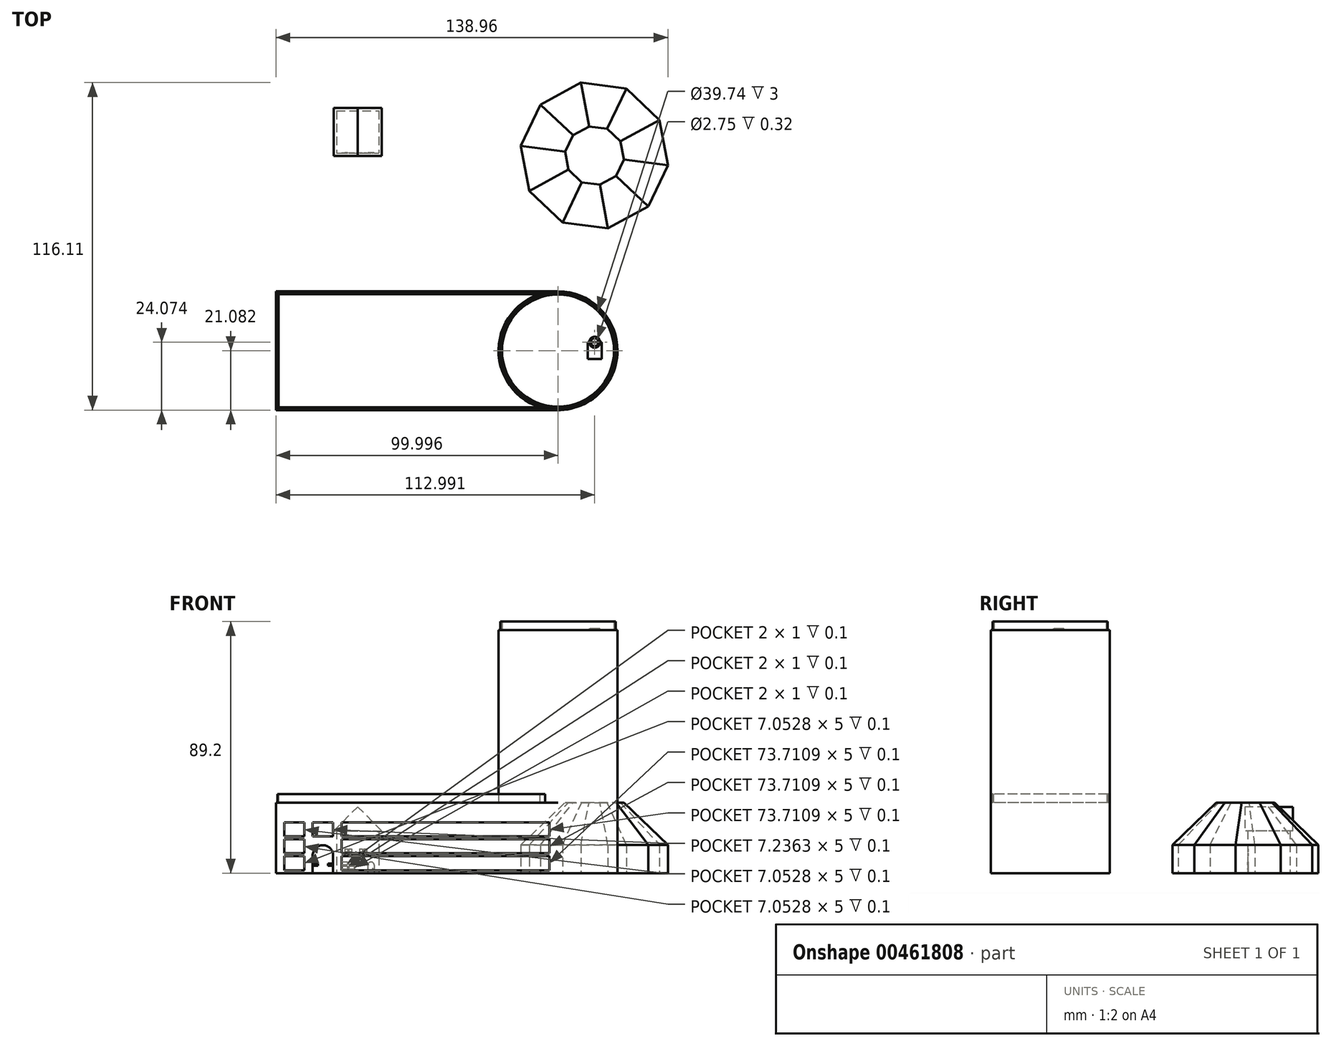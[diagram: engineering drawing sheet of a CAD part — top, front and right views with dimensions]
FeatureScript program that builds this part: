
annotation { "Feature Type Name" : "Feature", "Feature Type Description" : "" }
export const myFeature = defineFeature(function(context is Context, id is Id, definition is map)
    precondition{}
    {
        {
            var Q0;
            Q0=qCreatedBy(makeId("Top.planeOp"),FACE);
            var sketch = newSketch(context, id + "F0", { "sketchPlane" : qUnion([Q0])});
            skLineSegment(sketch, "E0.bottom", {"start": v(-51.13, 45.78) * mm, "end": v(-36.13, 45.78) * mm});
            skLineSegment(sketch, "E0.top", {"start": v(-51.13, 30.78) * mm, "end": v(-36.13, 30.78) * mm});
            skLineSegment(sketch, "E0.left", {"start": v(-51.13, 45.78) * mm, "end": v(-51.13, 30.78) * mm});
            skLineSegment(sketch, "E0.right", {"start": v(-36.13, 45.78) * mm, "end": v(-36.13, 30.78) * mm});
            skSolve(sketch);
        }
        {
            var Q0;
            Q0=makeQuery(id+"F0.imprint","IMPRINT",FACE,{"disambiguationData":[TD([[makeQuery(id+"F0.imprint","IMPRINT",EDGE,{"derivedFrom":sQuery(id+"F0.wireOp",EDGE,"E0.bottom")}),-1.0]])]});
            extrude(context, id + "F1", {"entities" : qUnion([Q0]), "depth" : 15 * mm});
        }
        {
            var Q0;
            Q0=makeQuery(id+"F1.opExtrude","SWEPT_FACE",FACE,{"disambiguationData":[OSD([sQuery(id+"F0.wireOp",EDGE,"E0.top")])]});
            var sketch = newSketch(context, id + "F2", { "sketchPlane" : qUnion([Q0])});
            skLineSegment(sketch, "E1.bottom", {"start": v(-49.33, 3.96) * mm, "end": v(-47.33, 3.96) * mm});
            skLineSegment(sketch, "E1.top", {"start": v(-49.33, 2.96) * mm, "end": v(-47.33, 2.96) * mm});
            skLineSegment(sketch, "E1.left", {"start": v(-49.33, 3.96) * mm, "end": v(-49.33, 2.96) * mm});
            skLineSegment(sketch, "E1.right", {"start": v(-47.33, 3.96) * mm, "end": v(-47.33, 2.96) * mm});
            skLineSegment(sketch, "E2.bottom", {"start": v(-46.83, 3.96) * mm, "end": v(-44.83, 3.96) * mm});
            skLineSegment(sketch, "E2.top", {"start": v(-46.83, 2.96) * mm, "end": v(-44.83, 2.96) * mm});
            skLineSegment(sketch, "E2.left", {"start": v(-46.83, 3.96) * mm, "end": v(-46.83, 2.96) * mm});
            skLineSegment(sketch, "E2.right", {"start": v(-44.83, 3.96) * mm, "end": v(-44.83, 2.96) * mm});
            skLineSegment(sketch, "E3.bottom", {"start": v(-49.33, 2.46) * mm, "end": v(-47.33, 2.46) * mm});
            skLineSegment(sketch, "E3.top", {"start": v(-49.33, 1.46) * mm, "end": v(-47.33, 1.46) * mm});
            skLineSegment(sketch, "E3.left", {"start": v(-49.33, 2.46) * mm, "end": v(-49.33, 1.46) * mm});
            skLineSegment(sketch, "E3.right", {"start": v(-47.33, 2.46) * mm, "end": v(-47.33, 1.46) * mm});
            skLineSegment(sketch, "E4.bottom", {"start": v(-46.83, 2.46) * mm, "end": v(-44.83, 2.46) * mm});
            skLineSegment(sketch, "E4.top", {"start": v(-46.83, 1.46) * mm, "end": v(-44.83, 1.46) * mm});
            skLineSegment(sketch, "E4.left", {"start": v(-46.83, 2.46) * mm, "end": v(-46.83, 1.46) * mm});
            skLineSegment(sketch, "E4.right", {"start": v(-44.83, 2.46) * mm, "end": v(-44.83, 1.46) * mm});
            skLineSegment(sketch, "E5.bottom", {"start": v(-48.24, 8.6) * mm, "end": v(-47.24, 8.6) * mm});
            skLineSegment(sketch, "E5.top", {"start": v(-48.24, 7.6) * mm, "end": v(-47.24, 7.6) * mm});
            skLineSegment(sketch, "E5.left", {"start": v(-48.24, 8.6) * mm, "end": v(-48.24, 7.6) * mm});
            skLineSegment(sketch, "E5.right", {"start": v(-47.24, 8.6) * mm, "end": v(-47.24, 7.6) * mm});
            skLineSegment(sketch, "E6.bottom", {"start": v(-46.75, 8.6) * mm, "end": v(-45.75, 8.6) * mm});
            skLineSegment(sketch, "E6.top", {"start": v(-46.75, 7.6) * mm, "end": v(-45.75, 7.6) * mm});
            skLineSegment(sketch, "E6.left", {"start": v(-46.75, 8.6) * mm, "end": v(-46.75, 7.6) * mm});
            skLineSegment(sketch, "E6.right", {"start": v(-45.75, 8.6) * mm, "end": v(-45.75, 7.6) * mm});
            skLineSegment(sketch, "E7.bottom", {"start": v(-47.25, 7.1) * mm, "end": v(-48.25, 7.1) * mm});
            skLineSegment(sketch, "E7.top", {"start": v(-47.25, 6.1) * mm, "end": v(-48.25, 6.1) * mm});
            skLineSegment(sketch, "E7.left", {"start": v(-47.25, 7.1) * mm, "end": v(-47.25, 6.1) * mm});
            skLineSegment(sketch, "E7.right", {"start": v(-48.25, 7.1) * mm, "end": v(-48.25, 6.1) * mm});
            skLineSegment(sketch, "E8.bottom", {"start": v(-46.75, 7.1) * mm, "end": v(-45.75, 7.1) * mm});
            skLineSegment(sketch, "E8.top", {"start": v(-46.75, 6.1) * mm, "end": v(-45.75, 6.1) * mm});
            skLineSegment(sketch, "E8.left", {"start": v(-46.75, 7.1) * mm, "end": v(-46.75, 6.1) * mm});
            skLineSegment(sketch, "E8.right", {"start": v(-45.75, 7.1) * mm, "end": v(-45.75, 6.1) * mm});
            skLineSegment(sketch, "E9.bottom", {"start": v(-42.98, 8.6) * mm, "end": v(-41.98, 8.6) * mm});
            skLineSegment(sketch, "E9.top", {"start": v(-42.98, 7.6) * mm, "end": v(-41.98, 7.6) * mm});
            skLineSegment(sketch, "E9.left", {"start": v(-42.98, 8.6) * mm, "end": v(-42.98, 7.6) * mm});
            skLineSegment(sketch, "E9.right", {"start": v(-41.98, 8.6) * mm, "end": v(-41.98, 7.6) * mm});
            skLineSegment(sketch, "E10.bottom", {"start": v(-41.48, 8.6) * mm, "end": v(-40.48, 8.6) * mm});
            skLineSegment(sketch, "E10.top", {"start": v(-41.48, 7.6) * mm, "end": v(-40.48, 7.6) * mm});
            skLineSegment(sketch, "E10.left", {"start": v(-41.48, 8.6) * mm, "end": v(-41.48, 7.6) * mm});
            skLineSegment(sketch, "E10.right", {"start": v(-40.48, 8.6) * mm, "end": v(-40.48, 7.6) * mm});
            skLineSegment(sketch, "E11.bottom", {"start": v(-42.98, 7.1) * mm, "end": v(-41.98, 7.1) * mm});
            skLineSegment(sketch, "E11.top", {"start": v(-42.98, 6.1) * mm, "end": v(-41.98, 6.1) * mm});
            skLineSegment(sketch, "E11.left", {"start": v(-42.98, 7.1) * mm, "end": v(-42.98, 6.1) * mm});
            skLineSegment(sketch, "E11.right", {"start": v(-41.98, 7.1) * mm, "end": v(-41.98, 6.1) * mm});
            skLineSegment(sketch, "E12.bottom", {"start": v(-41.48, 7.1) * mm, "end": v(-40.48, 7.1) * mm});
            skLineSegment(sketch, "E12.top", {"start": v(-41.48, 6.1) * mm, "end": v(-40.48, 6.1) * mm});
            skLineSegment(sketch, "E12.left", {"start": v(-41.48, 7.1) * mm, "end": v(-41.48, 6.1) * mm});
            skLineSegment(sketch, "E12.right", {"start": v(-40.48, 7.1) * mm, "end": v(-40.48, 6.1) * mm});
            skLineSegment(sketch, "E13", {"start": v(-40.05, 2.82) * mm, "end": v(-40.05, 0) * mm});
            skLineSegment(sketch, "E14", {"start": v(-37.79, 2.82) * mm, "end": v(-37.79, 0) * mm});
            skArc(sketch, "E15", {"start": v(-37.79, 2.82) * mm, "mid": v(-38.92, 3.95) * mm, "end": v(-40.05, 2.82) * mm});
            skCircle(sketch, "E16", {"center": v(-38.3, 1.47) * mm, "radius": 0.17 * mm});
            skSolve(sketch);
        }
        {
            var Q0;
            Q0=makeQuery(id+"F2.imprint","IMPRINT",FACE,{"disambiguationData":[TD([[makeQuery(id+"F2.imprint","IMPRINT",EDGE,{"derivedFrom":sQuery(id+"F2.wireOp",EDGE,"E2.bottom")}),-1.0]])]});
            var Q1;
            Q1=makeQuery(id+"F2.imprint","IMPRINT",FACE,{"disambiguationData":[TD([[makeQuery(id+"F2.imprint","IMPRINT",EDGE,{"derivedFrom":sQuery(id+"F2.wireOp",EDGE,"E3.bottom")}),-1.0]])]});
            var Q2;
            Q2=makeQuery(id+"F2.imprint","IMPRINT",FACE,{"disambiguationData":[TD([[makeQuery(id+"F2.imprint","IMPRINT",EDGE,{"derivedFrom":sQuery(id+"F2.wireOp",EDGE,"E4.bottom")}),-1.0]])]});
            var Q3;
            Q3=makeQuery(id+"F2.imprint","IMPRINT",FACE,{"disambiguationData":[TD([[makeQuery(id+"F2.imprint","IMPRINT",EDGE,{"derivedFrom":sQuery(id+"F2.wireOp",EDGE,"E7.bottom")}),1.0]])]});
            var Q4;
            Q4=makeQuery(id+"F2.imprint","IMPRINT",FACE,{"disambiguationData":[TD([[makeQuery(id+"F2.imprint","IMPRINT",EDGE,{"derivedFrom":sQuery(id+"F2.wireOp",EDGE,"E8.bottom")}),-1.0]])]});
            var Q5;
            Q5=makeQuery(id+"F2.imprint","IMPRINT",FACE,{"disambiguationData":[TD([[makeQuery(id+"F2.imprint","IMPRINT",EDGE,{"derivedFrom":sQuery(id+"F2.wireOp",EDGE,"E5.bottom")}),-1.0]])]});
            var Q6;
            Q6=makeQuery(id+"F2.imprint","IMPRINT",FACE,{"disambiguationData":[TD([[makeQuery(id+"F2.imprint","IMPRINT",EDGE,{"derivedFrom":sQuery(id+"F2.wireOp",EDGE,"E6.bottom")}),-1.0]])]});
            var Q7;
            Q7=makeQuery(id+"F2.imprint","IMPRINT",FACE,{"disambiguationData":[TD([[makeQuery(id+"F2.imprint","IMPRINT",EDGE,{"derivedFrom":sQuery(id+"F2.wireOp",EDGE,"E10.bottom")}),-1.0]])]});
            var Q8;
            Q8=makeQuery(id+"F2.imprint","IMPRINT",FACE,{"disambiguationData":[TD([[makeQuery(id+"F2.imprint","IMPRINT",EDGE,{"derivedFrom":sQuery(id+"F2.wireOp",EDGE,"E11.bottom")}),-1.0]])]});
            var Q9;
            Q9=makeQuery(id+"F2.imprint","IMPRINT",FACE,{"disambiguationData":[TD([[makeQuery(id+"F2.imprint","IMPRINT",EDGE,{"derivedFrom":sQuery(id+"F2.wireOp",EDGE,"E12.bottom")}),-1.0]])]});
            var Q10;
            {var subQ1=sQuery(id+"F2.wireOp",EDGE,"E13");Q10=makeQuery(id+"F2.imprint","IMPRINT",FACE,{"disambiguationData":[TD([[makeQuery(id+"F2.imprint","IMPRINT",EDGE,{"derivedFrom":subQ1}),1.0]])]});}
            var Q11;
            Q11=makeQuery(id+"F2.imprint","IMPRINT",FACE,{"disambiguationData":[TD([[makeQuery(id+"F2.imprint","IMPRINT",EDGE,{"derivedFrom":sQuery(id+"F2.wireOp",EDGE,"E1.bottom")}),-1.0]])]});
            var Q12;
            Q12=makeQuery(id+"F2.imprint","IMPRINT",FACE,{"disambiguationData":[TD([[makeQuery(id+"F2.imprint","IMPRINT",EDGE,{"derivedFrom":sQuery(id+"F2.wireOp",EDGE,"E9.bottom")}),-1.0]])]});
            extrude(context, id + "F3", {"entities" : qUnion([Q0, Q1, Q2, Q3, Q4, Q5, Q6, Q7, Q8, Q9, Q10, Q11, Q12]), "operationType" : NewBodyOperationType.REMOVE, "oppositeDirection" : true, "depth" : 0.1 * mm});
        }
        {
            var Q0;
            Q0=makeQuery(id+"F1.opExtrude","CAP_FACE",FACE,{"disambiguationData":[OSD([sQuery(id+"F0.wireOp",EDGE,"E0.bottom"),sQuery(id+"F0.wireOp",EDGE,"E0.top"),sQuery(id+"F0.wireOp",EDGE,"E0.left"),sQuery(id+"F0.wireOp",EDGE,"E0.right")])],"isStart":false});
            var sketch = newSketch(context, id + "F4", { "sketchPlane" : qUnion([Q0])});
            skLineSegment(sketch, "E17.bottom", {"start": v(-52.13, 46.78) * mm, "end": v(-35.13, 46.78) * mm});
            skLineSegment(sketch, "E17.top", {"start": v(-52.13, 29.78) * mm, "end": v(-35.13, 29.78) * mm});
            skLineSegment(sketch, "E17.left", {"start": v(-52.13, 46.78) * mm, "end": v(-52.13, 29.78) * mm});
            skLineSegment(sketch, "E17.right", {"start": v(-35.13, 46.78) * mm, "end": v(-35.13, 29.78) * mm});
            skSolve(sketch);
        }
        {
            var Q0;
            Q0=makeQuery(id+"F4.imprint","IMPRINT",FACE,{"disambiguationData":[TD([[makeQuery(id+"F4.imprint","IMPRINT",EDGE,{"derivedFrom":makeQuery(id+"F1.opExtrude","CAP_EDGE",EDGE,{"disambiguationData":[OSD([sQuery(id+"F0.wireOp",EDGE,"E0.bottom")])],"isStart":false})}),-1.0]])]});
            var Q1;
            Q1=makeQuery(id+"F4.imprint","IMPRINT",FACE,{"disambiguationData":[TD([[makeQuery(id+"F4.imprint","IMPRINT",EDGE,{"derivedFrom":sQuery(id+"F4.wireOp",EDGE,"E17.bottom")}),-1.0]])]});
            extrude(context, id + "F5", {"entities" : qUnion([Q0, Q1]), "operationType" : NewBodyOperationType.ADD, "depth" : 10 * mm});
        }
        {
            var Q0;
            Q0=makeQuery(id+"F5.opExtrude","CAP_EDGE",EDGE,{"disambiguationData":[OSD([sQuery(id+"F4.wireOp",EDGE,"E17.left")])],"isStart":false});
            var Q1;
            Q1=makeQuery(id+"F5.opExtrude","CAP_EDGE",EDGE,{"disambiguationData":[OSD([sQuery(id+"F4.wireOp",EDGE,"E17.right")])],"isStart":false});
            chamfer(context, id + "F6", {"entities" : qUnion([Q0, Q1]), "width" : 10 * mm, "tangentPropagation" : true});
        }
        {
            var Q0;
            Q0=qCreatedBy(makeId("Top.planeOp"),FACE);
            var sketch = newSketch(context, id + "F7", { "sketchPlane" : qUnion([Q0])});
            skLineSegment(sketch, "E18.bottom", {"start": v(-72.63, -18.2) * mm, "end": v(27.37, -18.2) * mm});
            skLineSegment(sketch, "E18.top", {"start": v(-72.63, -60.36) * mm, "end": v(27.37, -60.36) * mm});
            skLineSegment(sketch, "E18.left", {"start": v(-72.63, -18.2) * mm, "end": v(-72.63, -60.36) * mm});
            skLineSegment(sketch, "E18.right", {"start": v(27.37, -18.2) * mm, "end": v(27.37, -60.36) * mm, "construction": true});
            skArc(sketch, "E19", {"start": v(27.37, -60.36) * mm, "mid": v(48.45, -39.28) * mm, "end": v(27.37, -18.2) * mm});
            skSolve(sketch);
        }
        {
            var Q0;
            Q0=makeQuery(id+"F7.imprint","IMPRINT",FACE,{"disambiguationData":[TD([[makeQuery(id+"F7.imprint","IMPRINT",EDGE,{"derivedFrom":sQuery(id+"F7.wireOp",EDGE,"E18.bottom")}),-1.0]])]});
            extrude(context, id + "F8", {"entities" : qUnion([Q0]), "depth" : 25 * mm});
        }
        {
            var Q0;
            Q0=makeQuery(id+"F8.opExtrude","CAP_FACE",FACE,{"disambiguationData":[OSD([sQuery(id+"F7.wireOp",EDGE,"E18.bottom"),sQuery(id+"F7.wireOp",EDGE,"E18.top"),sQuery(id+"F7.wireOp",EDGE,"E18.left"),sQuery(id+"F7.wireOp",EDGE,"E19")])],"isStart":false});
            var sketch = newSketch(context, id + "F9", { "sketchPlane" : qUnion([Q0])});
            skCircle(sketch, "E20", {"center": v(27.37, -39.28) * mm, "radius": 21.08 * mm});
            skSolve(sketch);
        }
        {
            var Q0;
            {var subQ0=sQuery(id+"F9.wireOp",EDGE,"E20");var subQ1=makeQuery(id+"F9.imprint","INTERSECT",VERTEX,{"derivedFrom":[makeQuery(id+"F8.opExtrude","CAP_EDGE",EDGE,{"disambiguationData":[OSD([sQuery(id+"F7.wireOp",EDGE,"E18.bottom")])],"isStart":false}),subQ0]});Q0=makeQuery(id+"F9.imprint","IMPRINT",FACE,{"disambiguationData":[TD([[makeQuery(id+"F9.imprint","IMPRINT",EDGE,{"disambiguationData":[TD([[subQ1,1.0]])],"derivedFrom":subQ0}),1.0]])]});}
            extrude(context, id + "F10", {"entities" : qUnion([Q0]), "operationType" : NewBodyOperationType.ADD, "depth" : 61.2 * mm});
        }
        {
            var Q0;
            Q0=makeQuery(id+"F8.opExtrude","SWEPT_FACE",FACE,{"disambiguationData":[OSD([sQuery(id+"F7.wireOp",EDGE,"E18.top")])]});
            var sketch = newSketch(context, id + "F11", { "sketchPlane" : qUnion([Q0])});
            skLineSegment(sketch, "E21.bottom", {"start": v(-59.58, 6.26) * mm, "end": v(-52.34, 6.26) * mm});
            skLineSegment(sketch, "E21.top", {"start": v(-59.58, 0) * mm, "end": v(-52.34, 0) * mm});
            skLineSegment(sketch, "E21.left", {"start": v(-59.58, 6.26) * mm, "end": v(-59.58, 0) * mm});
            skLineSegment(sketch, "E21.right", {"start": v(-52.34, 6.26) * mm, "end": v(-52.34, 0) * mm});
            skArc(sketch, "E22", {"start": v(-52.34, 6.26) * mm, "mid": v(-55.96, 9.87) * mm, "end": v(-59.58, 6.26) * mm});
            skLineSegment(sketch, "E23.bottom", {"start": v(-59.28, 3.38) * mm, "end": v(-57.78, 3.38) * mm});
            skLineSegment(sketch, "E23.top", {"start": v(-59.28, 2.63) * mm, "end": v(-57.78, 2.63) * mm});
            skLineSegment(sketch, "E23.left", {"start": v(-59.28, 3.38) * mm, "end": v(-59.28, 2.63) * mm});
            skLineSegment(sketch, "E23.right", {"start": v(-57.78, 3.38) * mm, "end": v(-57.78, 2.63) * mm});
            skLineSegment(sketch, "E24.bottom", {"start": v(-54.14, 3.38) * mm, "end": v(-52.64, 3.38) * mm});
            skLineSegment(sketch, "E24.top", {"start": v(-54.14, 2.63) * mm, "end": v(-52.64, 2.63) * mm});
            skLineSegment(sketch, "E24.left", {"start": v(-54.14, 3.38) * mm, "end": v(-54.14, 2.63) * mm});
            skLineSegment(sketch, "E24.right", {"start": v(-52.64, 3.38) * mm, "end": v(-52.64, 2.63) * mm});
            skSolve(sketch);
        }
        {
            var Q0;
            Q0=makeQuery(id+"F11.imprint","IMPRINT",FACE,{"disambiguationData":[TD([[makeQuery(id+"F11.imprint","IMPRINT",EDGE,{"derivedFrom":sQuery(id+"F11.wireOp",EDGE,"E21.bottom")}),-1.0]])]});
            var Q1;
            Q1=makeQuery(id+"F11.imprint","IMPRINT",FACE,{"disambiguationData":[TD([[makeQuery(id+"F11.imprint","IMPRINT",EDGE,{"derivedFrom":sQuery(id+"F11.wireOp",EDGE,"E21.bottom")}),1.0]])]});
            extrude(context, id + "F12", {"entities" : qUnion([Q0, Q1]), "operationType" : NewBodyOperationType.REMOVE, "oppositeDirection" : true, "depth" : 0.1 * mm});
        }
        {
            var Q0;
            Q0=makeQuery(id+"F10.opExtrude","CAP_FACE",FACE,{"disambiguationData":[OSD([sQuery(id+"F9.wireOp",EDGE,"E20")])],"isStart":false});
            var sketch = newSketch(context, id + "F13", { "sketchPlane" : qUnion([Q0])});
            skCircle(sketch, "E25", {"center": v(27.37, -39.28) * mm, "radius": 20.41 * mm});
            skCircle(sketch, "E26", {"center": v(27.37, -39.28) * mm, "radius": 19.87 * mm});
            skSolve(sketch);
        }
        {
            var Q0;
            Q0=makeQuery(id+"F13.imprint","IMPRINT",FACE,{"disambiguationData":[TD([[makeQuery(id+"F13.imprint","IMPRINT",EDGE,{"derivedFrom":sQuery(id+"F13.wireOp",EDGE,"E25")}),1.0]])]});
            extrude(context, id + "F14", {"entities" : qUnion([Q0]), "operationType" : NewBodyOperationType.ADD, "depth" : 3 * mm});
        }
        {
            var Q0;
            Q0=makeQuery(id+"F14.boolean.opBoolean","SPLIT",FACE,{"disambiguationData":[TD([makeQuery(id+"F14.opExtrude","SWEPT_FACE",FACE,{"disambiguationData":[OSD([sQuery(id+"F13.wireOp",EDGE,"E26")])]})])],"derivedFrom":makeQuery(id+"F10.opExtrude","CAP_FACE",FACE,{"disambiguationData":[OSD([sQuery(id+"F9.wireOp",EDGE,"E20")])],"isStart":false})});
            var sketch = newSketch(context, id + "F15", { "sketchPlane" : qUnion([Q0])});
            skLineSegment(sketch, "E27.bottom", {"start": v(37.86, -36.29) * mm, "end": v(42.86, -36.29) * mm});
            skLineSegment(sketch, "E27.top", {"start": v(37.86, -42.29) * mm, "end": v(42.86, -42.29) * mm});
            skLineSegment(sketch, "E27.left", {"start": v(37.86, -36.29) * mm, "end": v(37.86, -42.29) * mm});
            skLineSegment(sketch, "E27.right", {"start": v(42.86, -36.29) * mm, "end": v(42.86, -42.29) * mm});
            skCircle(sketch, "E28", {"center": v(40.36, -36.29) * mm, "radius": 1.94 * mm});
            skCircle(sketch, "E29", {"center": v(40.36, -36.29) * mm, "radius": 1.37 * mm});
            skSolve(sketch);
        }
        {
            var Q0;
            {var subQ0=sQuery(id+"F15.wireOp",EDGE,"E29");var subQ1=sQuery(id+"F15.wireOp",EDGE,"E27.bottom");var subQ2=makeQuery(id+"F15.imprint","INTERSECT",VERTEX,{"disambiguationData":[OD(0.0)],"derivedFrom":[subQ1,subQ0]});Q0=makeQuery(id+"F15.imprint","IMPRINT",FACE,{"disambiguationData":[TD([[makeQuery(id+"F15.imprint","IMPRINT",EDGE,{"disambiguationData":[TD([[subQ2,-1.0]])],"derivedFrom":subQ1}),-1.0]])]});}
            var Q1;
            Q1=makeQuery(id+"F15.imprint","IMPRINT",FACE,{"disambiguationData":[TD([[makeQuery(id+"F15.imprint","IMPRINT",EDGE,{"derivedFrom":sQuery(id+"F15.wireOp",EDGE,"E27.top")}),1.0]])]});
            extrude(context, id + "F16", {"entities" : qUnion([Q0, Q1]), "operationType" : NewBodyOperationType.REMOVE, "oppositeDirection" : true, "depth" : 0.1 * mm});
        }
        {
            var Q0;
            Q0=makeQuery(id+"F14.boolean.opBoolean","SPLIT",FACE,{"disambiguationData":[TD([makeQuery(id+"F14.opExtrude","SWEPT_FACE",FACE,{"disambiguationData":[OSD([sQuery(id+"F13.wireOp",EDGE,"E26")])]})])],"derivedFrom":makeQuery(id+"F10.opExtrude","CAP_FACE",FACE,{"disambiguationData":[OSD([sQuery(id+"F9.wireOp",EDGE,"E20")])],"isStart":false})});
            var sketch = newSketch(context, id + "F17", { "sketchPlane" : qUnion([Q0])});
            skCircle(sketch, "E30", {"center": v(40.36, -36.29) * mm, "radius": 1.94 * mm});
            skCircle(sketch, "E31", {"center": v(40.36, -36.29) * mm, "radius": 1.37 * mm});
            skSolve(sketch);
        }
        {
            var Q0;
            {var subQ0=sQuery(id+"F17.wireOp",EDGE,"E30");var subQ1=sQuery(id+"F15.wireOp",EDGE,"E27.bottom");var subQ3=makeQuery(id+"F17.imprint","INTERSECT",VERTEX,{"derivedFrom":[makeQuery(id+"F16.boolean.opBoolean","COPY",EDGE,{"derivedFrom":makeQuery(id+"F16.opExtrude","CAP_EDGE",EDGE,{"disambiguationData":[OSD([subQ1]),TDD([makeQuery(id+"F15.imprint","IMPRINT",EDGE,{"disambiguationData":[TD([[makeQuery(id+"F15.imprint","INTERSECT",VERTEX,{"derivedFrom":[subQ1,sQuery(id+"F15.wireOp",EDGE,"E27.left")]}),-1.0]])],"derivedFrom":subQ1})])],"isStart":true})}),subQ0]});Q0=makeQuery(id+"F17.imprint","IMPRINT",FACE,{"disambiguationData":[TD([[makeQuery(id+"F17.imprint","IMPRINT",EDGE,{"disambiguationData":[TD([[subQ3,1.0]])],"derivedFrom":subQ0}),1.0]])]});}
            extrude(context, id + "F18", {"entities" : qUnion([Q0]), "operationType" : NewBodyOperationType.ADD, "depth" : 0.5 * mm});
        }
        {
            var Q0;
            Q0=makeQuery(id+"F18.opExtrude","CAP_EDGE",EDGE,{"disambiguationData":[OSD([sQuery(id+"F17.wireOp",EDGE,"E30")])],"isStart":false});
            var Q1;
            Q1=makeQuery(id+"F18.opExtrude","CAP_EDGE",EDGE,{"disambiguationData":[OSD([sQuery(id+"F17.wireOp",EDGE,"E31")])],"isStart":false});
            fillet(context, id + "F19", {"entities" : qUnion([Q0, Q1]), "radius" : 0.28 * mm, "tangentPropagation" : true, "allowEdgeOverflow" : false});
        }
        {
            var Q0;
            {var subQ1=sQuery(id+"F7.wireOp",EDGE,"E18.left");var subQ2=sQuery(id+"F7.wireOp",EDGE,"E18.top");Q0=makeQuery(id+"F12.boolean.opBoolean","SPLIT",FACE,{"disambiguationData":[TD([makeQuery(id+"F8.opExtrude","SWEPT_FACE",FACE,{"disambiguationData":[OSD([subQ1])]})])],"derivedFrom":makeQuery(id+"F8.opExtrude","SWEPT_FACE",FACE,{"disambiguationData":[OSD([subQ2])]})});}
            var sketch = newSketch(context, id + "F20", { "sketchPlane" : qUnion([Q0])});
            skLineSegment(sketch, "E32.bottom", {"start": v(-49.34, 6) * mm, "end": v(24.37, 6) * mm});
            skLineSegment(sketch, "E32.top", {"start": v(-49.34, 1) * mm, "end": v(24.37, 1) * mm});
            skLineSegment(sketch, "E32.left", {"start": v(-49.34, 6) * mm, "end": v(-49.34, 1) * mm});
            skLineSegment(sketch, "E32.right", {"start": v(24.37, 6) * mm, "end": v(24.37, 1) * mm});
            skLineSegment(sketch, "E33.bottom", {"start": v(-49.34, 18) * mm, "end": v(24.37, 18) * mm});
            skLineSegment(sketch, "E33.top", {"start": v(-49.34, 13) * mm, "end": v(24.37, 13) * mm});
            skLineSegment(sketch, "E33.left", {"start": v(-49.34, 18) * mm, "end": v(-49.34, 13) * mm});
            skLineSegment(sketch, "E33.right", {"start": v(24.37, 18) * mm, "end": v(24.37, 13) * mm});
            skLineSegment(sketch, "E34.bottom", {"start": v(24.37, 12) * mm, "end": v(-49.34, 12) * mm});
            skLineSegment(sketch, "E34.top", {"start": v(24.37, 7) * mm, "end": v(-49.34, 7) * mm});
            skLineSegment(sketch, "E34.left", {"start": v(24.37, 12) * mm, "end": v(24.37, 7) * mm});
            skLineSegment(sketch, "E34.right", {"start": v(-49.34, 12) * mm, "end": v(-49.34, 7) * mm});
            skLineSegment(sketch, "E35.bottom", {"start": v(-69.63, 6) * mm, "end": v(-62.58, 6) * mm});
            skLineSegment(sketch, "E35.top", {"start": v(-69.63, 1) * mm, "end": v(-62.58, 1) * mm});
            skLineSegment(sketch, "E35.left", {"start": v(-69.63, 6) * mm, "end": v(-69.63, 1) * mm});
            skLineSegment(sketch, "E35.right", {"start": v(-62.58, 6) * mm, "end": v(-62.58, 1) * mm});
            skLineSegment(sketch, "E36.bottom", {"start": v(-69.63, 12) * mm, "end": v(-62.58, 12) * mm});
            skLineSegment(sketch, "E36.top", {"start": v(-69.63, 7) * mm, "end": v(-62.58, 7) * mm});
            skLineSegment(sketch, "E36.left", {"start": v(-69.63, 12) * mm, "end": v(-69.63, 7) * mm});
            skLineSegment(sketch, "E36.right", {"start": v(-62.58, 12) * mm, "end": v(-62.58, 7) * mm});
            skLineSegment(sketch, "E37.bottom", {"start": v(-69.63, 18) * mm, "end": v(-62.58, 18) * mm});
            skLineSegment(sketch, "E37.top", {"start": v(-69.63, 13) * mm, "end": v(-62.58, 13) * mm});
            skLineSegment(sketch, "E37.left", {"start": v(-69.63, 18) * mm, "end": v(-69.63, 13) * mm});
            skLineSegment(sketch, "E37.right", {"start": v(-62.58, 18) * mm, "end": v(-62.58, 13) * mm});
            skLineSegment(sketch, "E38.bottom", {"start": v(-59.58, 18) * mm, "end": v(-52.34, 18) * mm});
            skLineSegment(sketch, "E38.top", {"start": v(-59.58, 13) * mm, "end": v(-52.34, 13) * mm});
            skLineSegment(sketch, "E38.left", {"start": v(-59.58, 18) * mm, "end": v(-59.58, 13) * mm});
            skLineSegment(sketch, "E38.right", {"start": v(-52.34, 18) * mm, "end": v(-52.34, 13) * mm});
            skSolve(sketch);
        }
        {
            var Q0;
            Q0=makeQuery(id+"F20.imprint","IMPRINT",FACE,{"disambiguationData":[TD([[makeQuery(id+"F20.imprint","IMPRINT",EDGE,{"derivedFrom":sQuery(id+"F20.wireOp",EDGE,"E35.bottom")}),-1.0]])]});
            var Q1;
            Q1=makeQuery(id+"F20.imprint","IMPRINT",FACE,{"disambiguationData":[TD([[makeQuery(id+"F20.imprint","IMPRINT",EDGE,{"derivedFrom":sQuery(id+"F20.wireOp",EDGE,"E36.bottom")}),-1.0]])]});
            var Q2;
            Q2=makeQuery(id+"F20.imprint","IMPRINT",FACE,{"disambiguationData":[TD([[makeQuery(id+"F20.imprint","IMPRINT",EDGE,{"derivedFrom":sQuery(id+"F20.wireOp",EDGE,"E37.bottom")}),-1.0]])]});
            var Q3;
            Q3=makeQuery(id+"F20.imprint","IMPRINT",FACE,{"disambiguationData":[TD([[makeQuery(id+"F20.imprint","IMPRINT",EDGE,{"derivedFrom":sQuery(id+"F20.wireOp",EDGE,"E38.bottom")}),-1.0]])]});
            var Q4;
            Q4=makeQuery(id+"F20.imprint","IMPRINT",FACE,{"disambiguationData":[TD([[makeQuery(id+"F20.imprint","IMPRINT",EDGE,{"derivedFrom":sQuery(id+"F20.wireOp",EDGE,"E33.bottom")}),-1.0]])]});
            var Q5;
            Q5=makeQuery(id+"F20.imprint","IMPRINT",FACE,{"disambiguationData":[TD([[makeQuery(id+"F20.imprint","IMPRINT",EDGE,{"derivedFrom":sQuery(id+"F20.wireOp",EDGE,"E34.bottom")}),1.0]])]});
            var Q6;
            Q6=makeQuery(id+"F20.imprint","IMPRINT",FACE,{"disambiguationData":[TD([[makeQuery(id+"F20.imprint","IMPRINT",EDGE,{"derivedFrom":sQuery(id+"F20.wireOp",EDGE,"E32.bottom")}),-1.0]])]});
            extrude(context, id + "F21", {"entities" : qUnion([Q0, Q1, Q2, Q3, Q4, Q5, Q6]), "operationType" : NewBodyOperationType.REMOVE, "oppositeDirection" : true, "depth" : 0.1 * mm});
        }
        {
            var Q0;
            Q0=makeQuery(id+"F8.opExtrude","CAP_FACE",FACE,{"disambiguationData":[OSD([sQuery(id+"F7.wireOp",EDGE,"E18.bottom"),sQuery(id+"F7.wireOp",EDGE,"E18.top"),sQuery(id+"F7.wireOp",EDGE,"E18.left"),sQuery(id+"F7.wireOp",EDGE,"E19")])],"isStart":false});
            var sketch = newSketch(context, id + "F22", { "sketchPlane" : qUnion([Q0])});
            skLineSegment(sketch, "E39.bottom", {"start": v(-72.13, -18.7) * mm, "end": v(22.8, -18.7) * mm});
            skLineSegment(sketch, "E39.top", {"start": v(-72.13, -59.86) * mm, "end": v(22.8, -59.86) * mm});
            skLineSegment(sketch, "E39.left", {"start": v(-72.13, -18.7) * mm, "end": v(-72.13, -59.86) * mm});
            skLineSegment(sketch, "E39.right", {"start": v(22.8, -18.7) * mm, "end": v(22.8, -59.86) * mm});
            skLineSegment(sketch, "E40.bottom", {"start": v(-71.63, -19.2) * mm, "end": v(20.95, -19.2) * mm});
            skLineSegment(sketch, "E40.top", {"start": v(-71.63, -59.36) * mm, "end": v(20.95, -59.36) * mm});
            skLineSegment(sketch, "E40.left", {"start": v(-71.63, -19.2) * mm, "end": v(-71.63, -59.36) * mm});
            skLineSegment(sketch, "E40.right", {"start": v(20.95, -19.2) * mm, "end": v(20.95, -59.36) * mm});
            skSolve(sketch);
        }
        {
            var Q0;
            {var subQ2=sQuery(id+"F22.wireOp",EDGE,"E39.bottom");Q0=makeQuery(id+"F22.imprint","IMPRINT",FACE,{"disambiguationData":[TD([[makeQuery(id+"F22.imprint","IMPRINT",EDGE,{"derivedFrom":subQ2}),-1.0]])]});}
            extrude(context, id + "F23", {"entities" : qUnion([Q0]), "operationType" : NewBodyOperationType.ADD, "depth" : 3 * mm});
        }
        {
            var Q0;
            Q0=qCreatedBy(makeId("Top.planeOp"),FACE);
            var sketch = newSketch(context, id + "F24", { "sketchPlane" : qUnion([Q0])});
            skCircle(sketch, "E41.cCircle", {"center": v(40.27, 29.9) * mm, "radius": 25 * mm, "construction": true});
            skLineSegment(sketch, "E41.0", {"start": v(35.48, 55.75) * mm, "end": v(51.58, 53.63) * mm});
            skLineSegment(sketch, "E41.1", {"start": v(51.58, 53.63) * mm, "end": v(63.37, 42.45) * mm});
            skLineSegment(sketch, "E41.2", {"start": v(63.37, 42.45) * mm, "end": v(66.33, 26.48) * mm});
            skLineSegment(sketch, "E41.3", {"start": v(66.33, 26.48) * mm, "end": v(59.34, 11.81) * mm});
            skLineSegment(sketch, "E41.4", {"start": v(59.34, 11.81) * mm, "end": v(45.06, 4.06) * mm});
            skLineSegment(sketch, "E41.5", {"start": v(45.06, 4.06) * mm, "end": v(28.96, 6.18) * mm});
            skLineSegment(sketch, "E41.6", {"start": v(28.96, 6.18) * mm, "end": v(17.17, 17.36) * mm});
            skLineSegment(sketch, "E41.7", {"start": v(17.17, 17.36) * mm, "end": v(14.2, 33.33) * mm});
            skLineSegment(sketch, "E41.8", {"start": v(14.2, 33.33) * mm, "end": v(21.2, 48) * mm});
            skLineSegment(sketch, "E41.9", {"start": v(21.2, 48) * mm, "end": v(35.48, 55.75) * mm});
            skPoint(sketch, "E41.0.midPoint", {"position": v(43.53, 54.7) * mm});
            skSolve(sketch);
        }
        {
            var Q0;
            Q0=makeQuery(id+"F24.imprint","IMPRINT",FACE,{"disambiguationData":[TD([[makeQuery(id+"F24.imprint","IMPRINT",EDGE,{"derivedFrom":sQuery(id+"F24.wireOp",EDGE,"E41.0")}),-1.0]])]});
            extrude(context, id + "F25", {"entities" : qUnion([Q0]), "depth" : 25 * mm});
        }
        {
            var Q0;
            Q0=makeQuery(id+"F25.opExtrude","CAP_EDGE",EDGE,{"disambiguationData":[OSD([sQuery(id+"F24.wireOp",EDGE,"E41.3")])],"isStart":false});
            var Q1;
            Q1=makeQuery(id+"F25.opExtrude","CAP_EDGE",EDGE,{"disambiguationData":[OSD([sQuery(id+"F24.wireOp",EDGE,"E41.2")])],"isStart":false});
            var Q2;
            Q2=makeQuery(id+"F25.opExtrude","CAP_EDGE",EDGE,{"disambiguationData":[OSD([sQuery(id+"F24.wireOp",EDGE,"E41.1")])],"isStart":false});
            var Q3;
            Q3=makeQuery(id+"F25.opExtrude","CAP_EDGE",EDGE,{"disambiguationData":[OSD([sQuery(id+"F24.wireOp",EDGE,"E41.0")])],"isStart":false});
            var Q4;
            Q4=makeQuery(id+"F25.opExtrude","CAP_EDGE",EDGE,{"disambiguationData":[OSD([sQuery(id+"F24.wireOp",EDGE,"E41.9")])],"isStart":false});
            var Q5;
            Q5=makeQuery(id+"F25.opExtrude","CAP_EDGE",EDGE,{"disambiguationData":[OSD([sQuery(id+"F24.wireOp",EDGE,"E41.8")])],"isStart":false});
            var Q6;
            Q6=makeQuery(id+"F25.opExtrude","CAP_EDGE",EDGE,{"disambiguationData":[OSD([sQuery(id+"F24.wireOp",EDGE,"E41.6")])],"isStart":false});
            var Q7;
            Q7=makeQuery(id+"F25.opExtrude","CAP_EDGE",EDGE,{"disambiguationData":[OSD([sQuery(id+"F24.wireOp",EDGE,"E41.5")])],"isStart":false});
            var Q8;
            Q8=makeQuery(id+"F25.opExtrude","CAP_EDGE",EDGE,{"disambiguationData":[OSD([sQuery(id+"F24.wireOp",EDGE,"E41.4")])],"isStart":false});
            var Q9;
            Q9=makeQuery(id+"F25.opExtrude","CAP_EDGE",EDGE,{"disambiguationData":[OSD([sQuery(id+"F24.wireOp",EDGE,"E41.7")])],"isStart":false});
            chamfer(context, id + "F26", {"entities" : qUnion([Q0, Q1, Q2, Q3, Q4, Q5, Q6, Q7, Q8, Q9]), "width" : 15 * mm, "tangentPropagation" : true});
        }
    });
